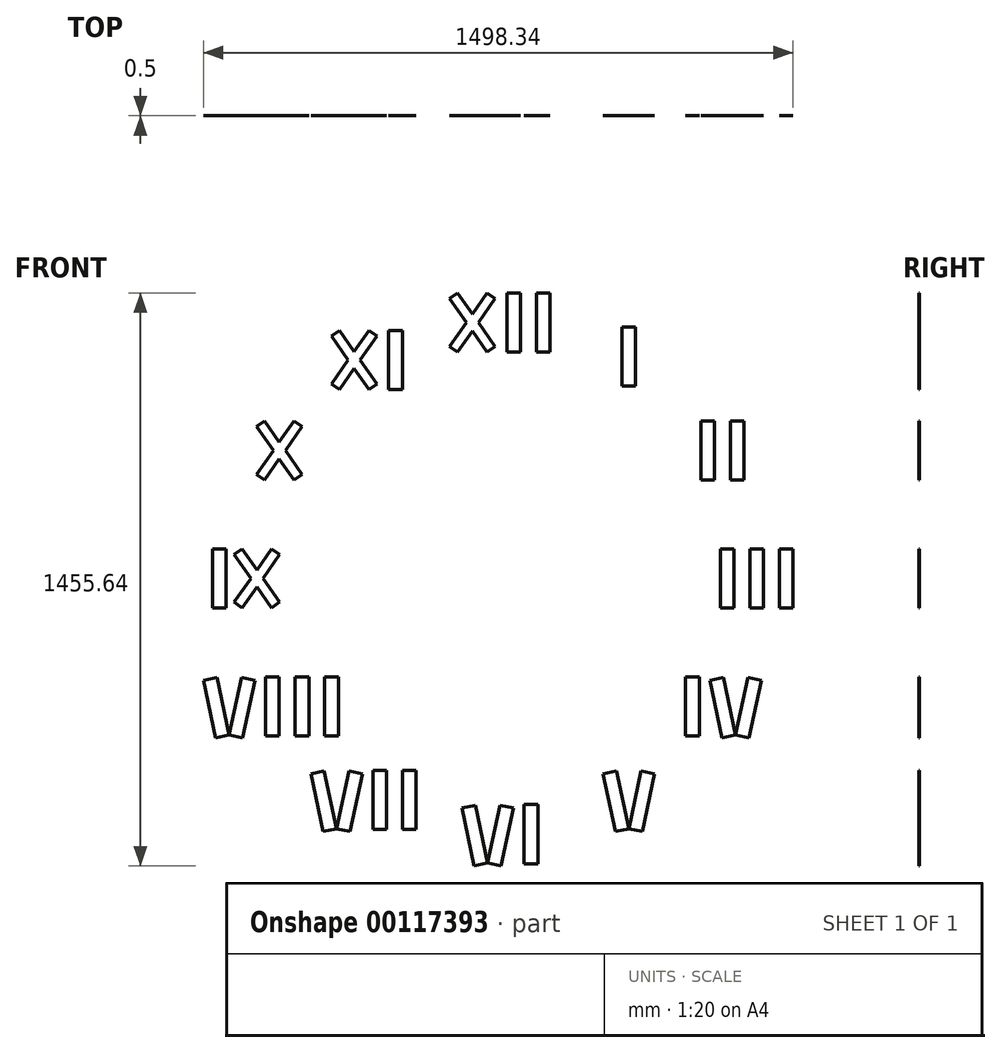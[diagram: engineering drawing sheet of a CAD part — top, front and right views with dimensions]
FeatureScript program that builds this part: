
annotation { "Feature Type Name" : "Feature", "Feature Type Description" : "" }
export const myFeature = defineFeature(function(context is Context, id is Id, definition is map)
    precondition{}
    {
        {
            var Q0;
            Q0=qCreatedBy(makeId("Front.planeOp"),FACE);
            var sketch = newSketch(context, id + "F0", { "sketchPlane" : qUnion([Q0])});
            skCircle(sketch, "E0", {"center": v(0, 0) * mm, "radius": 750 * mm, "construction": true});
            skCircle(sketch, "E1", {"center": v(0, 0) * mm, "radius": 600 * mm, "construction": true});
            skLineSegment(sketch, "E2", {"start": v(0, 750) * mm, "end": v(0, -750) * mm, "construction": true});
            skLineSegment(sketch, "E3", {"start": v(-750, 0) * mm, "end": v(750, 0) * mm, "construction": true});
            skLineSegment(sketch, "E4", {"start": v(375, 649.52) * mm, "end": v(-375, -649.52) * mm, "construction": true});
            skLineSegment(sketch, "E5", {"start": v(649.52, 375) * mm, "end": v(-649.52, -375) * mm, "construction": true});
            skLineSegment(sketch, "E6", {"start": v(649.52, -375) * mm, "end": v(-649.52, 375) * mm, "construction": true});
            skLineSegment(sketch, "E7", {"start": v(375, -649.52) * mm, "end": v(-375, 649.52) * mm, "construction": true});
            skPoint(sketch, "E8", {"position": v(300, 519.62) * mm});
            skPoint(sketch, "E9", {"position": v(0, 600) * mm});
            skPoint(sketch, "E10", {"position": v(519.62, 300) * mm});
            skPoint(sketch, "E11", {"position": v(-300, 519.62) * mm});
            skPoint(sketch, "E12", {"position": v(-519.62, 300) * mm});
            skPoint(sketch, "E13", {"position": v(-600, 0) * mm});
            skPoint(sketch, "E14", {"position": v(-519.62, -300) * mm});
            skPoint(sketch, "E15", {"position": v(-300, -519.62) * mm});
            skPoint(sketch, "E16", {"position": v(0, -600) * mm});
            skPoint(sketch, "E17", {"position": v(300, -519.62) * mm});
            skPoint(sketch, "E18", {"position": v(519.62, -300) * mm});
            skPoint(sketch, "E19", {"position": v(600, 0) * mm});
            skSolve(sketch);
        }
        {
            var Q0;
            Q0=qCreatedBy(makeId("Front.planeOp"),FACE);
            var sketch = newSketch(context, id + "F1", { "sketchPlane" : qUnion([Q0])});
            skLineSegment(sketch, "E20.bottom", {"start": v(307.5, 487.92) * mm, "end": v(342.5, 487.92) * mm});
            skLineSegment(sketch, "E20.top", {"start": v(307.5, 637.92) * mm, "end": v(342.5, 637.92) * mm});
            skLineSegment(sketch, "E20.left", {"start": v(307.5, 487.92) * mm, "end": v(307.5, 637.92) * mm});
            skLineSegment(sketch, "E20.right", {"start": v(342.5, 487.92) * mm, "end": v(342.5, 637.92) * mm});
            skLineSegment(sketch, "E21", {"start": v(325, 637.92) * mm, "end": v(325, 487.92) * mm, "construction": true});
            skLineSegment(sketch, "E22", {"start": v(307.5, 562.92) * mm, "end": v(342.5, 562.92) * mm, "construction": true});
            skPoint(sketch, "E23", {"position": v(325, 562.92) * mm});
            skSolve(sketch);
        }
        {
            var Q0;
            Q0=qCreatedBy(makeId("Front.planeOp"),FACE);
            var sketch = newSketch(context, id + "F2", { "sketchPlane" : qUnion([Q0])});
            skLineSegment(sketch, "E24.bottom", {"start": v(507.92, 400) * mm, "end": v(542.92, 400) * mm});
            skLineSegment(sketch, "E24.top", {"start": v(507.92, 250) * mm, "end": v(542.92, 250) * mm});
            skLineSegment(sketch, "E24.left", {"start": v(507.92, 400) * mm, "end": v(507.92, 250) * mm});
            skLineSegment(sketch, "E24.right", {"start": v(542.92, 400) * mm, "end": v(542.92, 250) * mm});
            skLineSegment(sketch, "E25.bottom", {"start": v(582.92, 400) * mm, "end": v(617.92, 400) * mm});
            skLineSegment(sketch, "E25.top", {"start": v(582.92, 250) * mm, "end": v(617.92, 250) * mm});
            skLineSegment(sketch, "E25.left", {"start": v(582.92, 400) * mm, "end": v(582.92, 250) * mm});
            skLineSegment(sketch, "E25.right", {"start": v(617.92, 400) * mm, "end": v(617.92, 250) * mm});
            skLineSegment(sketch, "E26", {"start": v(507.92, 325) * mm, "end": v(617.92, 325) * mm, "construction": true});
            skPoint(sketch, "E27", {"position": v(562.92, 325) * mm});
            skSolve(sketch);
        }
        {
            var Q0;
            Q0=qCreatedBy(makeId("Front.planeOp"),FACE);
            var sketch = newSketch(context, id + "F3", { "sketchPlane" : qUnion([Q0])});
            skLineSegment(sketch, "E28.bottom", {"start": v(557.5, 75) * mm, "end": v(592.5, 75) * mm});
            skLineSegment(sketch, "E28.top", {"start": v(557.5, -75) * mm, "end": v(592.5, -75) * mm});
            skLineSegment(sketch, "E28.left", {"start": v(557.5, 75) * mm, "end": v(557.5, -75) * mm});
            skLineSegment(sketch, "E28.right", {"start": v(592.5, 75) * mm, "end": v(592.5, -75) * mm});
            skLineSegment(sketch, "E29.bottom", {"start": v(632.5, 75) * mm, "end": v(667.5, 75) * mm});
            skLineSegment(sketch, "E29.top", {"start": v(632.5, -75) * mm, "end": v(667.5, -75) * mm});
            skLineSegment(sketch, "E29.left", {"start": v(632.5, 75) * mm, "end": v(632.5, -75) * mm});
            skLineSegment(sketch, "E29.right", {"start": v(667.5, 75) * mm, "end": v(667.5, -75) * mm});
            skLineSegment(sketch, "E30.bottom", {"start": v(707.5, 75) * mm, "end": v(742.5, 75) * mm});
            skLineSegment(sketch, "E30.top", {"start": v(707.5, -75) * mm, "end": v(742.5, -75) * mm});
            skLineSegment(sketch, "E30.left", {"start": v(707.5, 75) * mm, "end": v(707.5, -75) * mm});
            skLineSegment(sketch, "E30.right", {"start": v(742.5, 75) * mm, "end": v(742.5, -75) * mm});
            skLineSegment(sketch, "E31", {"start": v(557.5, 0) * mm, "end": v(632.5, 0) * mm, "construction": true});
            skLineSegment(sketch, "E32", {"start": v(632.5, 0) * mm, "end": v(667.5, 0) * mm, "construction": true});
            skLineSegment(sketch, "E33", {"start": v(667.5, 0) * mm, "end": v(742.5, 0) * mm, "construction": true});
            skPoint(sketch, "E34", {"position": v(650, 0) * mm});
            skSolve(sketch);
        }
        {
            var Q0;
            Q0=qCreatedBy(makeId("Front.planeOp"),FACE);
            var sketch = newSketch(context, id + "F4", { "sketchPlane" : qUnion([Q0])});
            skLineSegment(sketch, "E35.bottom", {"start": v(468.9, -250) * mm, "end": v(503.9, -250) * mm});
            skLineSegment(sketch, "E35.top", {"start": v(468.9, -400) * mm, "end": v(503.9, -400) * mm});
            skLineSegment(sketch, "E35.left", {"start": v(468.9, -250) * mm, "end": v(468.9, -400) * mm});
            skLineSegment(sketch, "E35.right", {"start": v(503.9, -250) * mm, "end": v(503.9, -400) * mm});
            skLineSegment(sketch, "E36.bottom", {"start": v(530.98, -258.92) * mm, "end": v(565.21, -251.64) * mm});
            skLineSegment(sketch, "E36.top", {"start": v(562.17, -405.64) * mm, "end": v(596.4, -398.36) * mm});
            skLineSegment(sketch, "E36.left", {"start": v(530.98, -258.92) * mm, "end": v(562.17, -405.64) * mm});
            skLineSegment(sketch, "E36.right", {"start": v(565.21, -251.64) * mm, "end": v(596.4, -398.36) * mm});
            skLineSegment(sketch, "E37.bottom", {"start": v(627.59, -251.64) * mm, "end": v(661.82, -258.92) * mm});
            skLineSegment(sketch, "E37.top", {"start": v(596.4, -398.36) * mm, "end": v(630.64, -405.64) * mm});
            skLineSegment(sketch, "E37.left", {"start": v(627.59, -251.64) * mm, "end": v(596.4, -398.36) * mm});
            skLineSegment(sketch, "E37.right", {"start": v(661.82, -258.92) * mm, "end": v(630.64, -405.64) * mm});
            skLineSegment(sketch, "E38", {"start": v(596.4, -251.64) * mm, "end": v(596.4, -405.64) * mm, "construction": true});
            skLineSegment(sketch, "E39", {"start": v(468.9, -325) * mm, "end": v(503.9, -325) * mm, "construction": true});
            skLineSegment(sketch, "E40", {"start": v(580.8, -325) * mm, "end": v(612, -325) * mm, "construction": true});
            skPoint(sketch, "E41", {"position": v(596.4, -325) * mm});
            skLineSegment(sketch, "E42", {"start": v(486.4, -250) * mm, "end": v(486.4, -400) * mm, "construction": true});
            skLineSegment(sketch, "E43", {"start": v(503.9, -325) * mm, "end": v(580.8, -325) * mm, "construction": true});
            skLineSegment(sketch, "E44", {"start": v(548.1, -255.28) * mm, "end": v(579.28, -402) * mm, "construction": true});
            skPoint(sketch, "E45", {"position": v(562.92, -325) * mm});
            skSolve(sketch);
        }
        {
            var Q0;
            Q0=qCreatedBy(makeId("Front.planeOp"),FACE);
            var sketch = newSketch(context, id + "F5", { "sketchPlane" : qUnion([Q0])});
            skLineSegment(sketch, "E46.bottom", {"start": v(259.58, -496.83) * mm, "end": v(293.81, -489.56) * mm});
            skLineSegment(sketch, "E46.top", {"start": v(290.76, -643.55) * mm, "end": v(325, -636.28) * mm});
            skLineSegment(sketch, "E46.left", {"start": v(259.58, -496.83) * mm, "end": v(290.76, -643.55) * mm});
            skLineSegment(sketch, "E46.right", {"start": v(293.81, -489.56) * mm, "end": v(325, -636.28) * mm});
            skLineSegment(sketch, "E47.bottom", {"start": v(356.19, -489.56) * mm, "end": v(390.42, -496.83) * mm});
            skLineSegment(sketch, "E47.top", {"start": v(325, -636.28) * mm, "end": v(359.24, -643.55) * mm});
            skLineSegment(sketch, "E47.left", {"start": v(356.19, -489.56) * mm, "end": v(325, -636.28) * mm});
            skLineSegment(sketch, "E47.right", {"start": v(390.42, -496.83) * mm, "end": v(359.24, -643.55) * mm});
            skLineSegment(sketch, "E48", {"start": v(325, -489.56) * mm, "end": v(325, -643.55) * mm, "construction": true});
            skLineSegment(sketch, "E49", {"start": v(309.4, -562.92) * mm, "end": v(340.6, -562.92) * mm, "construction": true});
            skPoint(sketch, "E50", {"position": v(325, -562.92) * mm});
            skSolve(sketch);
        }
        {
            var Q0;
            Q0=qCreatedBy(makeId("Front.planeOp"),FACE);
            var sketch = newSketch(context, id + "F6", { "sketchPlane" : qUnion([Q0])});
            skLineSegment(sketch, "E51.bottom", {"start": v(59.02, -575) * mm, "end": v(94.02, -575) * mm});
            skLineSegment(sketch, "E51.top", {"start": v(59.02, -725) * mm, "end": v(94.02, -725) * mm});
            skLineSegment(sketch, "E51.left", {"start": v(59.02, -575) * mm, "end": v(59.02, -725) * mm});
            skLineSegment(sketch, "E51.right", {"start": v(94.02, -575) * mm, "end": v(94.02, -725) * mm});
            skLineSegment(sketch, "E52.bottom", {"start": v(-98.9, -583.92) * mm, "end": v(-64.67, -576.64) * mm});
            skLineSegment(sketch, "E52.top", {"start": v(-67.72, -730.64) * mm, "end": v(-33.48, -723.36) * mm});
            skLineSegment(sketch, "E52.left", {"start": v(-98.9, -583.92) * mm, "end": v(-67.72, -730.64) * mm});
            skLineSegment(sketch, "E52.right", {"start": v(-64.67, -576.64) * mm, "end": v(-33.48, -723.36) * mm});
            skLineSegment(sketch, "E53.bottom", {"start": v(-2.3, -576.64) * mm, "end": v(31.94, -583.92) * mm});
            skLineSegment(sketch, "E53.top", {"start": v(-33.48, -723.36) * mm, "end": v(0.75, -730.64) * mm});
            skLineSegment(sketch, "E53.left", {"start": v(-2.3, -576.64) * mm, "end": v(-33.48, -723.36) * mm});
            skLineSegment(sketch, "E53.right", {"start": v(31.94, -583.92) * mm, "end": v(0.75, -730.64) * mm});
            skLineSegment(sketch, "E54", {"start": v(-33.48, -576.64) * mm, "end": v(-33.48, -723.36) * mm, "construction": true});
            skLineSegment(sketch, "E55", {"start": v(59.02, -650) * mm, "end": v(94.02, -650) * mm, "construction": true});
            skLineSegment(sketch, "E56", {"start": v(-49.08, -650) * mm, "end": v(-17.9, -650) * mm, "construction": true});
            skPoint(sketch, "E57", {"position": v(-33.48, -650) * mm});
            skLineSegment(sketch, "E58", {"start": v(76.52, -575) * mm, "end": v(76.52, -725) * mm, "construction": true});
            skLineSegment(sketch, "E59", {"start": v(14.82, -580.28) * mm, "end": v(-16.37, -727) * mm, "construction": true});
            skLineSegment(sketch, "E60", {"start": v(59.02, -650) * mm, "end": v(-17.9, -650) * mm, "construction": true});
            skPoint(sketch, "E61", {"position": v(0, -650) * mm});
            skSolve(sketch);
        }
        {
            var Q0;
            Q0=qCreatedBy(makeId("Front.planeOp"),FACE);
            var sketch = newSketch(context, id + "F7", { "sketchPlane" : qUnion([Q0])});
            skLineSegment(sketch, "E62.bottom", {"start": v(-325, -487.92) * mm, "end": v(-290, -487.92) * mm});
            skLineSegment(sketch, "E62.top", {"start": v(-325, -637.92) * mm, "end": v(-290, -637.92) * mm});
            skLineSegment(sketch, "E62.left", {"start": v(-325, -487.92) * mm, "end": v(-325, -637.92) * mm});
            skLineSegment(sketch, "E62.right", {"start": v(-290, -487.92) * mm, "end": v(-290, -637.92) * mm});
            skLineSegment(sketch, "E63.bottom", {"start": v(-482.92, -496.83) * mm, "end": v(-448.69, -489.56) * mm});
            skLineSegment(sketch, "E63.top", {"start": v(-451.74, -643.55) * mm, "end": v(-417.5, -636.28) * mm});
            skLineSegment(sketch, "E63.left", {"start": v(-482.92, -496.83) * mm, "end": v(-451.74, -643.55) * mm});
            skLineSegment(sketch, "E63.right", {"start": v(-448.69, -489.56) * mm, "end": v(-417.5, -636.28) * mm});
            skLineSegment(sketch, "E64.bottom", {"start": v(-386.31, -489.56) * mm, "end": v(-352.08, -496.83) * mm});
            skLineSegment(sketch, "E64.top", {"start": v(-417.5, -636.28) * mm, "end": v(-383.26, -643.55) * mm});
            skLineSegment(sketch, "E64.left", {"start": v(-386.31, -489.56) * mm, "end": v(-417.5, -636.28) * mm});
            skLineSegment(sketch, "E64.right", {"start": v(-352.08, -496.83) * mm, "end": v(-383.26, -643.55) * mm});
            skLineSegment(sketch, "E65", {"start": v(-417.5, -489.56) * mm, "end": v(-417.5, -636.28) * mm, "construction": true});
            skLineSegment(sketch, "E66", {"start": v(-325, -562.92) * mm, "end": v(-290, -562.92) * mm, "construction": true});
            skLineSegment(sketch, "E67", {"start": v(-433.1, -562.92) * mm, "end": v(-401.9, -562.92) * mm, "construction": true});
            skPoint(sketch, "E68", {"position": v(-417.5, -562.92) * mm});
            skLineSegment(sketch, "E69", {"start": v(-307.5, -487.92) * mm, "end": v(-307.5, -637.92) * mm, "construction": true});
            skLineSegment(sketch, "E70", {"start": v(-369.2, -493.2) * mm, "end": v(-400.38, -639.92) * mm, "construction": true});
            skLineSegment(sketch, "E71", {"start": v(-325, -562.92) * mm, "end": v(-401.9, -562.92) * mm, "construction": true});
            skPoint(sketch, "E72", {"position": v(-384.02, -562.92) * mm});
            skLineSegment(sketch, "E73.right", {"start": v(-215, -487.92) * mm, "end": v(-215, -637.92) * mm});
            skLineSegment(sketch, "E73.left", {"start": v(-250, -487.92) * mm, "end": v(-250, -637.92) * mm});
            skLineSegment(sketch, "E73.top", {"start": v(-250, -637.92) * mm, "end": v(-215, -637.92) * mm});
            skLineSegment(sketch, "E73.bottom", {"start": v(-250, -487.92) * mm, "end": v(-215, -487.92) * mm});
            skLineSegment(sketch, "E74", {"start": v(-232.5, -487.92) * mm, "end": v(-232.5, -637.92) * mm, "construction": true});
            skLineSegment(sketch, "E75", {"start": v(-250, -562.92) * mm, "end": v(-215, -562.92) * mm, "construction": true});
            skLineSegment(sketch, "E76", {"start": v(-290, -562.92) * mm, "end": v(-250, -562.92) * mm, "construction": true});
            skSolve(sketch);
        }
        {
            var Q0;
            Q0=qCreatedBy(makeId("Front.planeOp"),FACE);
            var sketch = newSketch(context, id + "F8", { "sketchPlane" : qUnion([Q0])});
            skLineSegment(sketch, "E77.bottom", {"start": v(-597.92, -250) * mm, "end": v(-562.92, -250) * mm});
            skLineSegment(sketch, "E77.top", {"start": v(-597.92, -400) * mm, "end": v(-562.92, -400) * mm});
            skLineSegment(sketch, "E77.left", {"start": v(-597.92, -250) * mm, "end": v(-597.92, -400) * mm});
            skLineSegment(sketch, "E77.right", {"start": v(-562.92, -250) * mm, "end": v(-562.92, -400) * mm});
            skLineSegment(sketch, "E78.bottom", {"start": v(-755.84, -258.92) * mm, "end": v(-721.6, -251.64) * mm});
            skLineSegment(sketch, "E78.top", {"start": v(-724.65, -405.64) * mm, "end": v(-690.42, -398.36) * mm});
            skLineSegment(sketch, "E78.left", {"start": v(-755.84, -258.92) * mm, "end": v(-724.65, -405.64) * mm});
            skLineSegment(sketch, "E78.right", {"start": v(-721.6, -251.64) * mm, "end": v(-690.42, -398.36) * mm});
            skLineSegment(sketch, "E79.bottom", {"start": v(-659.23, -251.64) * mm, "end": v(-625, -258.92) * mm});
            skLineSegment(sketch, "E79.top", {"start": v(-690.42, -398.36) * mm, "end": v(-656.18, -405.64) * mm});
            skLineSegment(sketch, "E79.left", {"start": v(-659.23, -251.64) * mm, "end": v(-690.42, -398.36) * mm});
            skLineSegment(sketch, "E79.right", {"start": v(-625, -258.92) * mm, "end": v(-656.18, -405.64) * mm});
            skLineSegment(sketch, "E80", {"start": v(-690.42, -251.64) * mm, "end": v(-690.42, -398.36) * mm, "construction": true});
            skLineSegment(sketch, "E81", {"start": v(-597.92, -325) * mm, "end": v(-562.92, -325) * mm, "construction": true});
            skLineSegment(sketch, "E82", {"start": v(-706, -325) * mm, "end": v(-674.82, -325) * mm, "construction": true});
            skPoint(sketch, "E83", {"position": v(-690.42, -325) * mm});
            skLineSegment(sketch, "E84", {"start": v(-580.42, -250) * mm, "end": v(-580.42, -400) * mm, "construction": true});
            skLineSegment(sketch, "E85", {"start": v(-642.11, -255.28) * mm, "end": v(-673.3, -402) * mm, "construction": true});
            skLineSegment(sketch, "E86", {"start": v(-597.92, -325) * mm, "end": v(-674.82, -325) * mm, "construction": true});
            skPoint(sketch, "E87", {"position": v(-656.93, -325) * mm});
            skLineSegment(sketch, "E88.right", {"start": v(-487.92, -250) * mm, "end": v(-487.92, -400) * mm});
            skLineSegment(sketch, "E88.left", {"start": v(-522.92, -250) * mm, "end": v(-522.92, -400) * mm});
            skLineSegment(sketch, "E88.top", {"start": v(-522.92, -400) * mm, "end": v(-487.92, -400) * mm});
            skLineSegment(sketch, "E88.bottom", {"start": v(-522.92, -250) * mm, "end": v(-487.92, -250) * mm});
            skLineSegment(sketch, "E89", {"start": v(-505.42, -250) * mm, "end": v(-505.42, -400) * mm, "construction": true});
            skLineSegment(sketch, "E90", {"start": v(-522.92, -325) * mm, "end": v(-487.92, -325) * mm, "construction": true});
            skLineSegment(sketch, "E91", {"start": v(-562.92, -325) * mm, "end": v(-522.92, -325) * mm, "construction": true});
            skLineSegment(sketch, "E92", {"start": v(-447.92, -325) * mm, "end": v(-412.92, -325) * mm, "construction": true});
            skLineSegment(sketch, "E93.left", {"start": v(-447.92, -250) * mm, "end": v(-447.92, -400) * mm});
            skLineSegment(sketch, "E94", {"start": v(-430.42, -250) * mm, "end": v(-430.42, -400) * mm, "construction": true});
            skLineSegment(sketch, "E93.right", {"start": v(-412.92, -250) * mm, "end": v(-412.92, -400) * mm});
            skLineSegment(sketch, "E93.top", {"start": v(-447.92, -400) * mm, "end": v(-412.92, -400) * mm});
            skLineSegment(sketch, "E93.bottom", {"start": v(-447.92, -250) * mm, "end": v(-412.92, -250) * mm});
            skLineSegment(sketch, "E95", {"start": v(-487.92, -325) * mm, "end": v(-447.92, -325) * mm, "construction": true});
            skSolve(sketch);
        }
        {
            var Q0;
            Q0=qCreatedBy(makeId("Front.planeOp"),FACE);
            var sketch = newSketch(context, id + "F9", { "sketchPlane" : qUnion([Q0])});
            skLineSegment(sketch, "E96.bottom", {"start": v(-677.73, 60.66) * mm, "end": v(-657.26, 75) * mm});
            skLineSegment(sketch, "E96.top", {"start": v(-582.74, -75) * mm, "end": v(-562.27, -60.66) * mm});
            skLineSegment(sketch, "E96.left", {"start": v(-677.73, 60.66) * mm, "end": v(-582.74, -75) * mm});
            skLineSegment(sketch, "E96.right", {"start": v(-657.26, 75) * mm, "end": v(-562.27, -60.66) * mm});
            skLineSegment(sketch, "E97", {"start": v(-667.5, 67.83) * mm, "end": v(-572.5, -67.83) * mm, "construction": true});
            skPoint(sketch, "E98", {"position": v(-620, 0) * mm});
            skLineSegment(sketch, "E99.bottom", {"start": v(-732.73, 75) * mm, "end": v(-697.73, 75) * mm});
            skLineSegment(sketch, "E99.top", {"start": v(-732.73, -75) * mm, "end": v(-697.73, -75) * mm});
            skLineSegment(sketch, "E99.left", {"start": v(-732.73, 75) * mm, "end": v(-732.73, -75) * mm});
            skLineSegment(sketch, "E99.right", {"start": v(-697.73, 75) * mm, "end": v(-697.73, -75) * mm});
            skLineSegment(sketch, "E100", {"start": v(-715.23, 75) * mm, "end": v(-715.23, -75) * mm, "construction": true});
            skPoint(sketch, "E101", {"position": v(-715.23, 0) * mm});
            skLineSegment(sketch, "E102.bottom", {"start": v(-562.27, 60.66) * mm, "end": v(-582.74, 75) * mm});
            skLineSegment(sketch, "E102.top", {"start": v(-608.15, -4.87) * mm, "end": v(-628.63, 9.47) * mm});
            skLineSegment(sketch, "E102.left", {"start": v(-562.27, 60.66) * mm, "end": v(-608.15, -4.87) * mm});
            skLineSegment(sketch, "E102.right", {"start": v(-582.74, 75) * mm, "end": v(-628.63, 9.47) * mm});
            skLineSegment(sketch, "E103", {"start": v(-572.5, 67.83) * mm, "end": v(-618.4, 2.3) * mm, "construction": true});
            skLineSegment(sketch, "E104.right", {"start": v(-631.85, 4.87) * mm, "end": v(-677.73, -60.66) * mm});
            skLineSegment(sketch, "E104.bottom", {"start": v(-611.37, -9.47) * mm, "end": v(-631.85, 4.87) * mm});
            skLineSegment(sketch, "E104.left", {"start": v(-611.37, -9.47) * mm, "end": v(-657.26, -75) * mm});
            skLineSegment(sketch, "E104.top", {"start": v(-657.26, -75) * mm, "end": v(-677.73, -60.66) * mm});
            skLineSegment(sketch, "E105", {"start": v(-621.6, -2.3) * mm, "end": v(-667.5, -67.83) * mm, "construction": true});
            skSolve(sketch);
        }
        {
            var Q0;
            Q0=qCreatedBy(makeId("Front.planeOp"),FACE);
            var sketch = newSketch(context, id + "F10", { "sketchPlane" : qUnion([Q0])});
            skLineSegment(sketch, "E106.bottom", {"start": v(-620.65, 385.66) * mm, "end": v(-600.17, 400) * mm});
            skLineSegment(sketch, "E106.top", {"start": v(-525.66, 250) * mm, "end": v(-505.18, 264.34) * mm});
            skLineSegment(sketch, "E106.left", {"start": v(-620.65, 385.66) * mm, "end": v(-525.66, 250) * mm});
            skLineSegment(sketch, "E106.right", {"start": v(-600.17, 400) * mm, "end": v(-505.18, 264.34) * mm});
            skLineSegment(sketch, "E107", {"start": v(-610.41, 392.83) * mm, "end": v(-515.42, 257.17) * mm, "construction": true});
            skPoint(sketch, "E108", {"position": v(-562.92, 325) * mm});
            skLineSegment(sketch, "E109.bottom", {"start": v(-505.18, 385.66) * mm, "end": v(-525.66, 400) * mm});
            skLineSegment(sketch, "E109.top", {"start": v(-551.07, 320.13) * mm, "end": v(-571.55, 334.47) * mm});
            skLineSegment(sketch, "E109.left", {"start": v(-505.18, 385.66) * mm, "end": v(-551.07, 320.13) * mm});
            skLineSegment(sketch, "E109.right", {"start": v(-525.66, 400) * mm, "end": v(-571.55, 334.47) * mm});
            skLineSegment(sketch, "E110", {"start": v(-515.42, 392.83) * mm, "end": v(-561.3, 327.3) * mm, "construction": true});
            skLineSegment(sketch, "E111.right", {"start": v(-574.77, 329.87) * mm, "end": v(-620.65, 264.34) * mm});
            skLineSegment(sketch, "E111.bottom", {"start": v(-554.29, 315.53) * mm, "end": v(-574.77, 329.87) * mm});
            skLineSegment(sketch, "E111.left", {"start": v(-554.29, 315.53) * mm, "end": v(-600.17, 250) * mm});
            skLineSegment(sketch, "E111.top", {"start": v(-600.17, 250) * mm, "end": v(-620.65, 264.34) * mm});
            skLineSegment(sketch, "E112", {"start": v(-564.53, 322.7) * mm, "end": v(-610.41, 257.17) * mm, "construction": true});
            skSolve(sketch);
        }
        {
            var Q0;
            Q0=qCreatedBy(makeId("Front.planeOp"),FACE);
            var sketch = newSketch(context, id + "F11", { "sketchPlane" : qUnion([Q0])});
            skLineSegment(sketch, "E113.bottom", {"start": v(-430.35, 614.92) * mm, "end": v(-409.87, 629.26) * mm});
            skLineSegment(sketch, "E113.top", {"start": v(-335.36, 479.26) * mm, "end": v(-314.88, 493.6) * mm});
            skLineSegment(sketch, "E113.left", {"start": v(-430.35, 614.92) * mm, "end": v(-335.36, 479.26) * mm});
            skLineSegment(sketch, "E113.right", {"start": v(-409.87, 629.26) * mm, "end": v(-314.88, 493.6) * mm});
            skLineSegment(sketch, "E114", {"start": v(-420.11, 622.09) * mm, "end": v(-325.12, 486.43) * mm, "construction": true});
            skPoint(sketch, "E115", {"position": v(-372.62, 554.26) * mm});
            skLineSegment(sketch, "E116.bottom", {"start": v(-284.88, 629.26) * mm, "end": v(-249.88, 629.26) * mm});
            skLineSegment(sketch, "E116.top", {"start": v(-284.88, 479.26) * mm, "end": v(-249.88, 479.26) * mm});
            skLineSegment(sketch, "E116.left", {"start": v(-284.88, 629.26) * mm, "end": v(-284.88, 479.26) * mm});
            skLineSegment(sketch, "E116.right", {"start": v(-249.88, 629.26) * mm, "end": v(-249.88, 479.26) * mm});
            skLineSegment(sketch, "E117", {"start": v(-267.38, 629.26) * mm, "end": v(-267.38, 479.26) * mm, "construction": true});
            skPoint(sketch, "E118", {"position": v(-267.38, 554.26) * mm});
            skLineSegment(sketch, "E119.bottom", {"start": v(-314.88, 614.92) * mm, "end": v(-335.36, 629.26) * mm});
            skLineSegment(sketch, "E119.top", {"start": v(-360.77, 549.38) * mm, "end": v(-381.25, 563.72) * mm});
            skLineSegment(sketch, "E119.left", {"start": v(-314.88, 614.92) * mm, "end": v(-360.77, 549.38) * mm});
            skLineSegment(sketch, "E119.right", {"start": v(-335.36, 629.26) * mm, "end": v(-381.25, 563.72) * mm});
            skLineSegment(sketch, "E120", {"start": v(-325.12, 622.09) * mm, "end": v(-371, 556.55) * mm, "construction": true});
            skLineSegment(sketch, "E121.right", {"start": v(-384.47, 559.13) * mm, "end": v(-430.35, 493.6) * mm});
            skLineSegment(sketch, "E121.bottom", {"start": v(-363.99, 544.79) * mm, "end": v(-384.47, 559.13) * mm});
            skLineSegment(sketch, "E121.left", {"start": v(-363.99, 544.79) * mm, "end": v(-409.87, 479.26) * mm});
            skLineSegment(sketch, "E121.top", {"start": v(-409.87, 479.26) * mm, "end": v(-430.35, 493.6) * mm});
            skLineSegment(sketch, "E122", {"start": v(-374.23, 551.96) * mm, "end": v(-420.11, 486.43) * mm, "construction": true});
            skLineSegment(sketch, "E123", {"start": v(-372.62, 554.26) * mm, "end": v(-267.38, 554.26) * mm, "construction": true});
            skPoint(sketch, "E124", {"position": v(-320, 554.26) * mm});
            skSolve(sketch);
        }
        {
            var Q0;
            Q0=qCreatedBy(makeId("Front.planeOp"),FACE);
            var sketch = newSketch(context, id + "F12", { "sketchPlane" : qUnion([Q0])});
            skLineSegment(sketch, "E125.bottom", {"start": v(-130.35, 710.66) * mm, "end": v(-109.87, 725) * mm});
            skLineSegment(sketch, "E125.top", {"start": v(-35.36, 575) * mm, "end": v(-14.88, 589.34) * mm});
            skLineSegment(sketch, "E125.left", {"start": v(-130.35, 710.66) * mm, "end": v(-35.36, 575) * mm});
            skLineSegment(sketch, "E125.right", {"start": v(-109.87, 725) * mm, "end": v(-14.88, 589.34) * mm});
            skLineSegment(sketch, "E126", {"start": v(-120.11, 717.83) * mm, "end": v(-25.12, 582.17) * mm, "construction": true});
            skPoint(sketch, "E127", {"position": v(-72.62, 650) * mm});
            skLineSegment(sketch, "E128.bottom", {"start": v(15.12, 725) * mm, "end": v(50.12, 725) * mm});
            skLineSegment(sketch, "E128.top", {"start": v(15.12, 575) * mm, "end": v(50.12, 575) * mm});
            skLineSegment(sketch, "E128.left", {"start": v(15.12, 725) * mm, "end": v(15.12, 575) * mm});
            skLineSegment(sketch, "E128.right", {"start": v(50.12, 725) * mm, "end": v(50.12, 575) * mm});
            skLineSegment(sketch, "E129", {"start": v(32.62, 725) * mm, "end": v(32.62, 575) * mm, "construction": true});
            skPoint(sketch, "E130", {"position": v(32.62, 650) * mm});
            skLineSegment(sketch, "E131.bottom", {"start": v(-14.88, 710.66) * mm, "end": v(-35.36, 725) * mm});
            skLineSegment(sketch, "E131.top", {"start": v(-60.77, 645.13) * mm, "end": v(-81.25, 659.47) * mm});
            skLineSegment(sketch, "E131.left", {"start": v(-14.88, 710.66) * mm, "end": v(-60.77, 645.13) * mm});
            skLineSegment(sketch, "E131.right", {"start": v(-35.36, 725) * mm, "end": v(-81.25, 659.47) * mm});
            skLineSegment(sketch, "E132", {"start": v(-25.12, 717.83) * mm, "end": v(-71, 652.3) * mm, "construction": true});
            skLineSegment(sketch, "E133.right", {"start": v(-84.47, 654.87) * mm, "end": v(-130.35, 589.34) * mm});
            skLineSegment(sketch, "E133.bottom", {"start": v(-63.99, 640.53) * mm, "end": v(-84.47, 654.87) * mm});
            skLineSegment(sketch, "E133.left", {"start": v(-63.99, 640.53) * mm, "end": v(-109.87, 575) * mm});
            skLineSegment(sketch, "E133.top", {"start": v(-109.87, 575) * mm, "end": v(-130.35, 589.34) * mm});
            skLineSegment(sketch, "E134", {"start": v(-74.23, 647.7) * mm, "end": v(-120.11, 582.17) * mm, "construction": true});
            skLineSegment(sketch, "E135", {"start": v(-72.62, 650) * mm, "end": v(32.62, 650) * mm, "construction": true});
            skPoint(sketch, "E136", {"position": v(-20, 650) * mm});
            skPoint(sketch, "E137", {"position": v(107.62, 650) * mm});
            skLineSegment(sketch, "E138", {"start": v(107.62, 725) * mm, "end": v(107.62, 575) * mm, "construction": true});
            skLineSegment(sketch, "E139.right", {"start": v(125.12, 725) * mm, "end": v(125.12, 575) * mm});
            skLineSegment(sketch, "E139.left", {"start": v(90.12, 725) * mm, "end": v(90.12, 575) * mm});
            skLineSegment(sketch, "E139.top", {"start": v(90.12, 575) * mm, "end": v(125.12, 575) * mm});
            skLineSegment(sketch, "E139.bottom", {"start": v(90.12, 725) * mm, "end": v(125.12, 725) * mm});
            skSolve(sketch);
        }
        {
            var Q0;
            Q0=qSketchRegion(id+"F1",true);
            var Q1;
            Q1=qSketchRegion(id+"F2",true);
            var Q2;
            Q2=qSketchRegion(id+"F3",true);
            var Q3;
            Q3=qSketchRegion(id+"F4",true);
            var Q4;
            Q4=qSketchRegion(id+"F5",true);
            var Q5;
            Q5=qSketchRegion(id+"F6",true);
            var Q6;
            Q6=qSketchRegion(id+"F7",true);
            var Q7;
            Q7=qSketchRegion(id+"F8",true);
            var Q8;
            Q8=qSketchRegion(id+"F9",true);
            var Q9;
            Q9=qSketchRegion(id+"F10",true);
            var Q10;
            Q10=qSketchRegion(id+"F11",true);
            var Q11;
            Q11=qSketchRegion(id+"F12",true);
            extrude(context, id + "F13", {"entities" : qUnion([Q0, Q1, Q2, Q3, Q4, Q5, Q6, Q7, Q8, Q9, Q10, Q11]), "depth" : 0.5 * mm});
        }
    });
